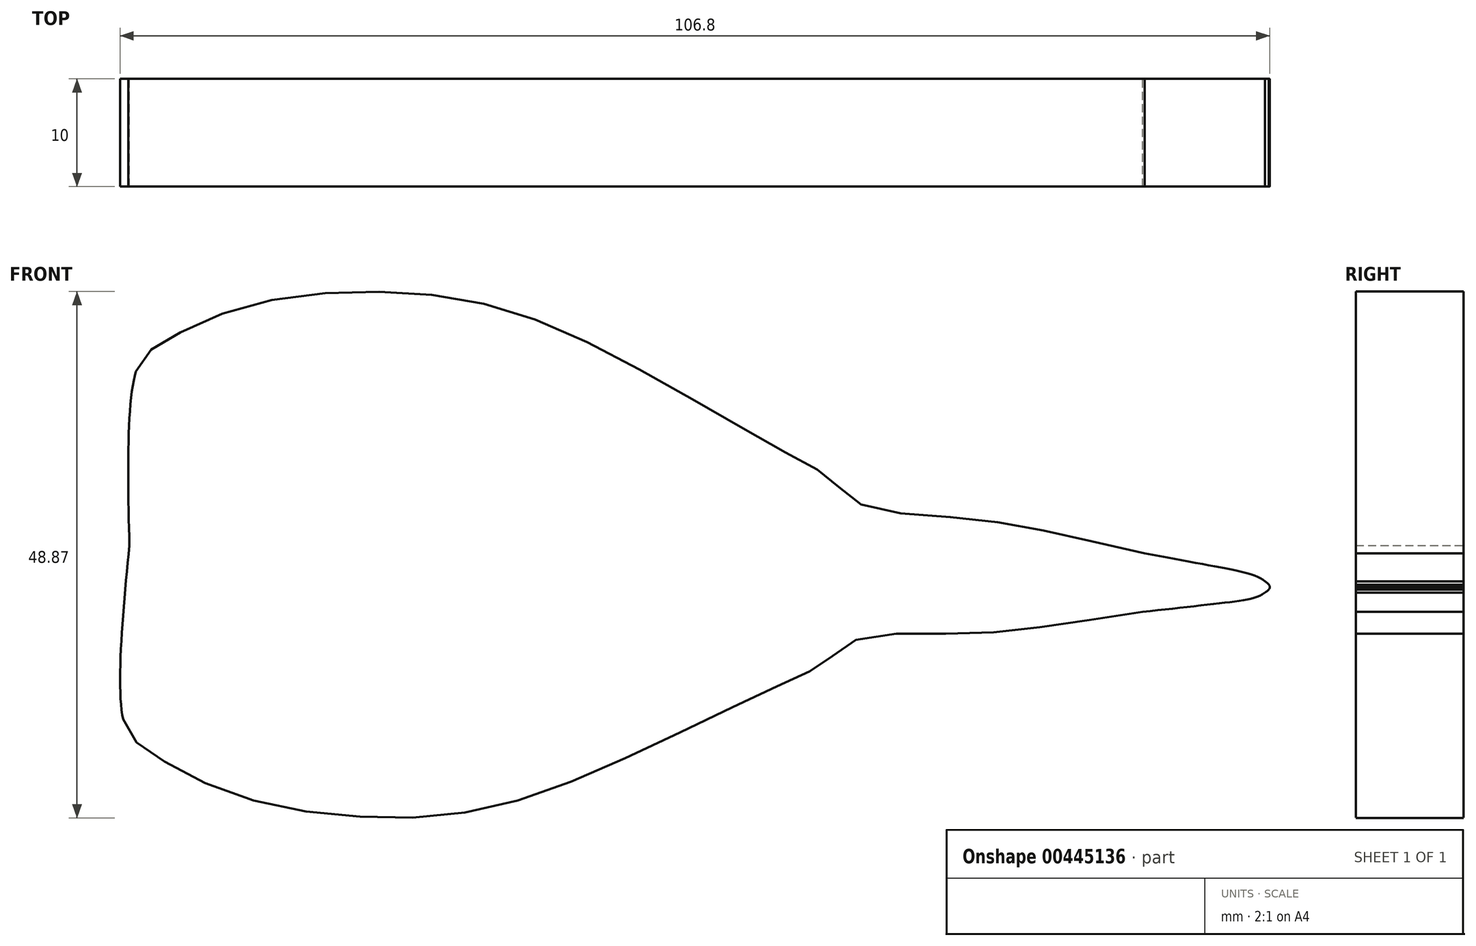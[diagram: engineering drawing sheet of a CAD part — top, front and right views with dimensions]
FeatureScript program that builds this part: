
annotation { "Feature Type Name" : "Feature", "Feature Type Description" : "" }
export const myFeature = defineFeature(function(context is Context, id is Id, definition is map)
    precondition{}
    {
        {
            var Q0;
            Q0=qCreatedBy(makeId("Front.planeOp"),FACE);
            var sketch = newSketch(context, id + "F0", { "sketchPlane" : qUnion([Q0])});
            skFitSpline(sketch, "E0", {"points": [v(-27.62, -19.6) * mm, v(-43.48, -13.41) * mm, v(-43.9, -10.12) * mm, v(-43.88, 3.18) * mm, v(-43.27, 19.33) * mm, v(-41.21, 21.8) * mm, v(-33.39, 25.3) * mm, v(-20.62, 26.74) * mm, v(-8.27, 24.89) * mm, v(5.32, 18.5) * mm, v(17.27, 11.7) * mm, v(21.39, 9.24) * mm, v(24.06, 6.97) * mm, v(33.33, 5.74) * mm, v(43.22, 4.1) * mm, v(55.41, 1.37) * mm, v(61.32, 0) * mm, v(61.98, -0.48) * mm, v(62.05, -0.7) * mm, v(61.25, -1.42) * mm, v(57.39, -2.2) * mm, v(45.24, -3.56) * mm, v(37.37, -4.24) * mm, v(29.6, -4.34) * mm, v(25.12, -4.92) * mm], "startDerivative": vector(-316.3, 102.27) * mm, "endDerivative": vector(-119.29, -21.02) * mm});
            skLineSegment(sketch, "E1", {"start": v(-43.88, 3.18) * mm, "end": v(62.05, -0.7) * mm});
            skFitSpline(sketch, "E2.MirrorCS", {"points": [v(-26, 24.7) * mm, v(-42.27, 19.7) * mm, v(-42.92, 16.44) * mm, v(-43.88, 3.18) * mm, v(-44.46, -12.97) * mm, v(-42.59, -15.59) * mm, v(-35.04, -19.65) * mm, v(-22.41, -22.02) * mm, v(-9.95, -21.08) * mm, v(4.07, -15.71) * mm, v(16.48, -9.8) * mm, v(20.77, -7.65) * mm, v(23.6, -5.58) * mm, v(32.94, -5.03) * mm, v(42.91, -4.11) * mm, v(55.28, -2.29) * mm, v(61.27, -1.36) * mm, v(61.96, -0.93) * mm, v(62.05, -0.7) * mm, v(61.3, 0.06) * mm, v(57.5, 1.12) * mm, v(45.5, 3.37) * mm, v(37.7, 4.63) * mm, v(29.94, 5.3) * mm, v(25.53, 6.2) * mm], "startDerivative": vector(-322.93, -78.82) * mm, "endDerivative": vector(-117.43, 29.7) * mm});
            skLineSegment(sketch, "E3", {"start": v(-43.27, 19.33) * mm, "end": v(-44.46, -12.97) * mm});
            skLineSegment(sketch, "E4", {"start": v(61.98, -0.48) * mm, "end": v(61.96, -0.93) * mm});
            skSolve(sketch);
        }
        {
            var Q0;
            Q0=qSketchRegion(id+"F0",true);
            extrude(context, id + "F1", {"entities" : qUnion([Q0]), "depth" : 10 * mm});
        }
    });
